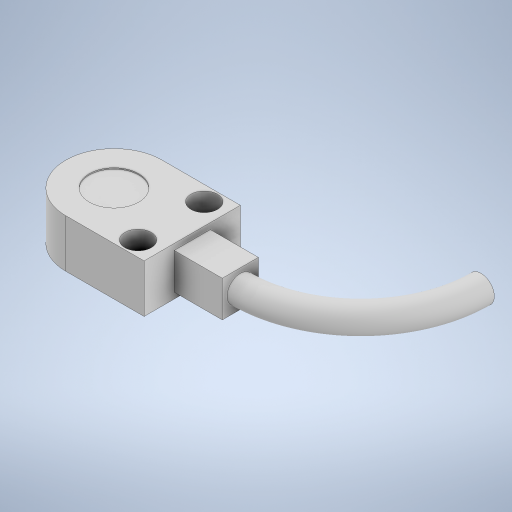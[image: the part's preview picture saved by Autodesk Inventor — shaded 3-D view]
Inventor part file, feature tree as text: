
AUTODESK INVENTOR PART (.ipt)
format: ipt  version: 2023 (Build 270158000, 158)  size: 299,520 bytes
history: native  units: mm
features: sketch x6, extrude x3, plane x3, revolve x1
ambient origin geometry x8: Origin, YZ Plane, XZ Plane, XY Plane, X Axis, Y Axis, Z Axis, Center Point
bodies: Solid1 (feature_tree)
feature tree (13):
  extrude  "Extrusion1"  Depth=8.0mm
  extrude  "Extrusion2"  Depth=5.5mm
  extrude  "Extrusion3"  Depth=1.75mm
  sketch  "Sketch4"  dims[d6=2.2mm d7=2.2mm]
  plane  "Work Plane2"
  sketch  "Sketch5"  dims[d8=4.0mm d9=0.0mm]
  plane  "Work Plane3"
  sketch  "Sketch6"  dims[d10=3.0mm d11=3.0mm d12=0.5mm d13=5.5mm d14=4.0mm d15=0.0mm d16=4.1mm d17=0.1mm d18=0.0mm d19=2.2mm d22=-10.0mm d23=10.0mm d24=2.2mm d25=20.0mm d26=10.0mm d27=90.0deg]
  revolve  "Revolution1"  [1 undecoded]
  sketch  "Sketch1"  dims[d0=8.0mm d1=6.5mm]
  sketch  "Sketch2"  dims[d2=5.5mm d3=2.75mm]
  sketch  "Sketch3"  dims[d4=1.75mm d5=1.75mm]
  plane  "Work Plane1"
note: 1 required parameter value undecoded (feature->parameter linkage not recoverable at this tier; creation-order binding heuristic only, values carry confidence <= 0.55)
